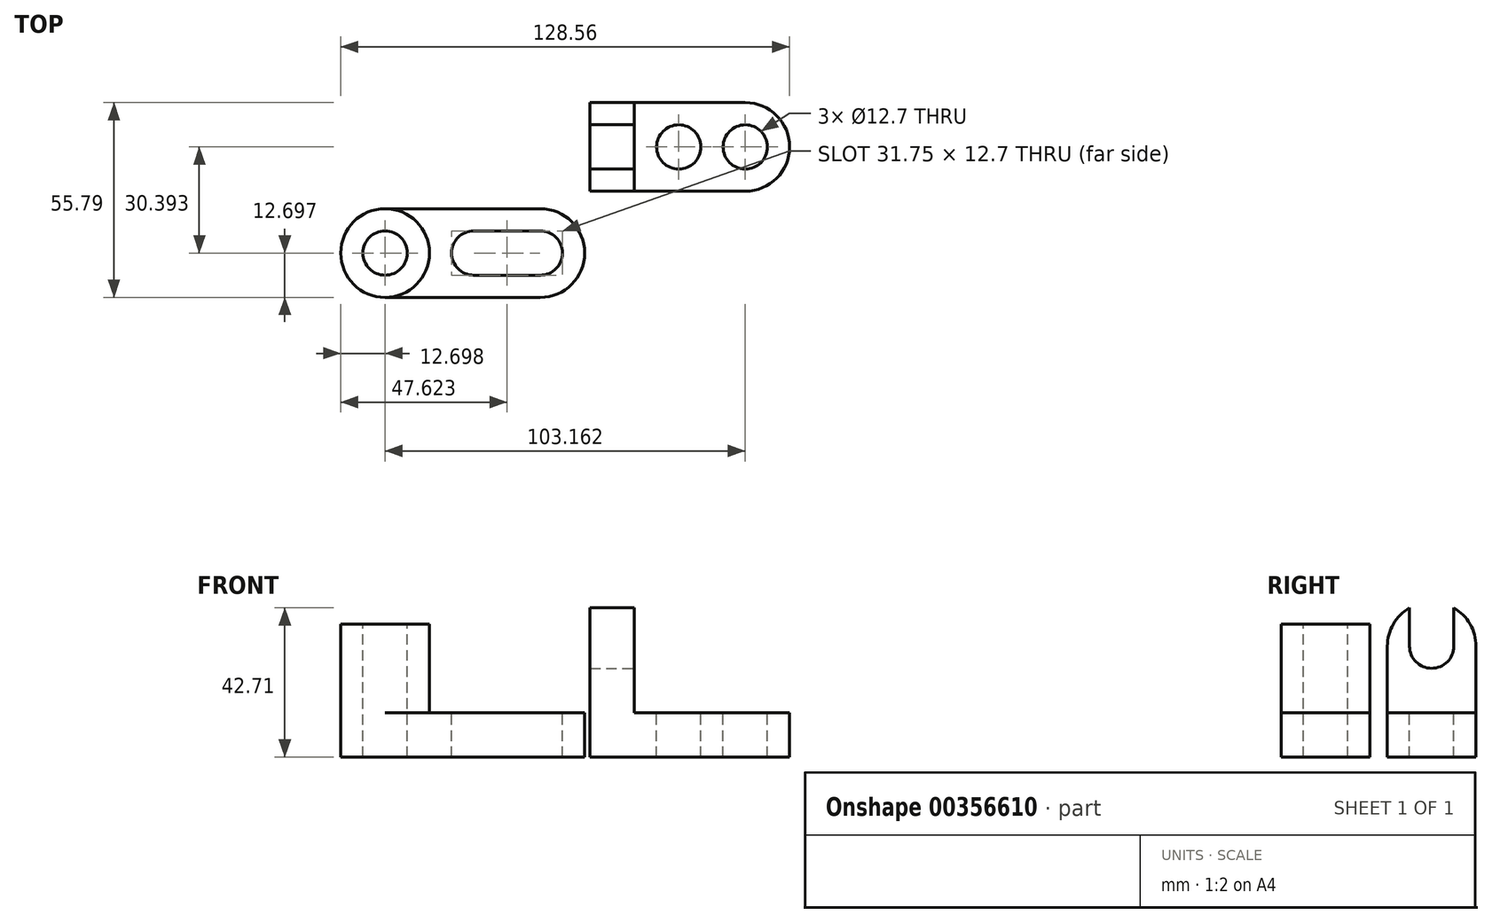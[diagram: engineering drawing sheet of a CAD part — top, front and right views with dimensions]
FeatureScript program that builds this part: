
annotation { "Feature Type Name" : "Feature", "Feature Type Description" : "" }
export const myFeature = defineFeature(function(context is Context, id is Id, definition is map)
    precondition{}
    {
        {
            var Q0;
            Q0=qCreatedBy(makeId("Front.planeOp"),FACE);
            var sketch = newSketch(context, id + "F0", { "sketchPlane" : qUnion([Q0])});
            skLineSegment(sketch, "E0", {"start": v(0, 0) * mm, "end": v(0, 44.45) * mm});
            skLineSegment(sketch, "E1", {"start": v(0, 44.45) * mm, "end": v(12.7, 44.45) * mm});
            skLineSegment(sketch, "E2", {"start": v(12.7, 44.45) * mm, "end": v(12.7, 12.7) * mm});
            skLineSegment(sketch, "E3", {"start": v(12.7, 12.7) * mm, "end": v(57.15, 12.7) * mm});
            skLineSegment(sketch, "E4", {"start": v(57.15, 12.7) * mm, "end": v(57.15, 0) * mm});
            skLineSegment(sketch, "E5", {"start": v(57.15, 0) * mm, "end": v(0, 0) * mm});
            skSolve(sketch);
        }
        {
            var Q0;
            Q0 = qSketchRegion(id + "F0", true);
            extrude(context, id + "F1", {"entities" : qUnion([Q0]), "depth" : 25.4 * mm});
        }
        {
            var Q0;
            Q0=makeQuery(id+"F1.opExtrude","SWEPT_FACE",FACE,{"disambiguationData":[OSD([sQuery(id+"F0.wireOp",EDGE,"E3")])]});
            var sketch = newSketch(context, id + "F2", { "sketchPlane" : qUnion([Q0])});
            skCircle(sketch, "E6", {"center": v(25.4, -12.7) * mm, "radius": 6.35 * mm});
            skCircle(sketch, "E7", {"center": v(44.45, -12.7) * mm, "radius": 6.35 * mm});
            skArc(sketch, "E8", {"start": v(44.45, -25.4) * mm, "mid": v(57.15, -12.7) * mm, "end": v(44.45, 0) * mm});
            skSolve(sketch);
        }
        {
            var Q0;
            Q0=makeQuery(id+"F2.imprint","IMPRINT",FACE,{"disambiguationData":[TD([[makeQuery(id+"F2.imprint","IMPRINT",EDGE,{"derivedFrom":sQuery(id+"F2.wireOp",EDGE,"E6")}),1.0]])]});
            var Q1;
            Q1=makeQuery(id+"F2.imprint","IMPRINT",FACE,{"disambiguationData":[TD([[makeQuery(id+"F2.imprint","IMPRINT",EDGE,{"derivedFrom":sQuery(id+"F2.wireOp",EDGE,"E7")}),1.0]])]});
            var Q2;
            {var subQ0=sQuery(id+"F2.wireOp",EDGE,"E8");var subQ1=sQuery(id+"F0.wireOp",EDGE,"E3");var subQ2=makeQuery(id+"F1.opExtrude","CAP_EDGE",EDGE,{"disambiguationData":[OSD([subQ1])],"isStart":true});var subQ3=makeQuery(id+"F2.imprint","INTERSECT",VERTEX,{"derivedFrom":[subQ2,subQ0]});Q2=makeQuery(id+"F2.imprint","IMPRINT",FACE,{"disambiguationData":[TD([[makeQuery(id+"F2.imprint","IMPRINT",EDGE,{"disambiguationData":[TD([[subQ3,1.0]])],"derivedFrom":subQ0}),-1.0]])]});}
            var Q3;
            {var subQ0=sQuery(id+"F2.wireOp",EDGE,"E8");var subQ1=sQuery(id+"F0.wireOp",EDGE,"E3");var subQ2=makeQuery(id+"F1.opExtrude","CAP_EDGE",EDGE,{"disambiguationData":[OSD([subQ1])],"isStart":false});var subQ3=makeQuery(id+"F2.imprint","INTERSECT",VERTEX,{"derivedFrom":[subQ2,subQ0]});Q3=makeQuery(id+"F2.imprint","IMPRINT",FACE,{"disambiguationData":[TD([[makeQuery(id+"F2.imprint","IMPRINT",EDGE,{"disambiguationData":[TD([[subQ3,-1.0]])],"derivedFrom":subQ0}),-1.0]])]});}
            extrude(context, id + "F3", {"entities" : qUnion([Q0, Q1, Q2, Q3]), "operationType" : NewBodyOperationType.REMOVE, "oppositeDirection" : true, "depth" : 12.7 * mm});
        }
        {
            var Q0;
            Q0=makeQuery(id+"F1.opExtrude","SWEPT_FACE",FACE,{"disambiguationData":[OSD([sQuery(id+"F0.wireOp",EDGE,"E2")])]});
            var sketch = newSketch(context, id + "F4", { "sketchPlane" : qUnion([Q0])});
            skCircle(sketch, "E9", {"center": v(-12.7, 31.75) * mm, "radius": 6.35 * mm});
            skLineSegment(sketch, "E10", {"start": v(-19.05, 31.75) * mm, "end": v(-19.05, 44.45) * mm});
            skLineSegment(sketch, "E11", {"start": v(-6.35, 31.75) * mm, "end": v(-6.35, 44.45) * mm});
            skArc(sketch, "E12", {"start": v(0, 31.75) * mm, "mid": v(-12.7, 44.4) * mm, "end": v(-25.4, 31.75) * mm});
            skSolve(sketch);
        }
        {
            var Q0;
            Q0 = qSketchRegion(id + "F4", true);
            var Q1;
            {var subQ0=sQuery(id+"F4.wireOp",EDGE,"E10");Q1=makeQuery(id+"F4.imprint","IMPRINT",FACE,{"disambiguationData":[TD([[makeQuery(id+"F4.imprint","IMPRINT",EDGE,{"derivedFrom":subQ0}),-1.0]])]});}
            var Q2;
            {var subQ1=sQuery(id+"F0.wireOp",EDGE,"E2");var subQ4=sQuery(id+"F4.wireOp",EDGE,"E12");var subQ6=makeQuery(id+"F1.opExtrude","CAP_EDGE",EDGE,{"disambiguationData":[OSD([subQ1])],"isStart":true});var subQ8=makeQuery(id+"F4.imprint","INTERSECT",VERTEX,{"derivedFrom":[subQ6,subQ4]});Q2=makeQuery(id+"F4.imprint","IMPRINT",FACE,{"disambiguationData":[TD([[makeQuery(id+"F4.imprint","IMPRINT",EDGE,{"disambiguationData":[TD([[subQ8,-1.0]])],"derivedFrom":subQ4}),-1.0]])]});}
            var Q3;
            {var subQ1=sQuery(id+"F0.wireOp",EDGE,"E2");var subQ4=sQuery(id+"F4.wireOp",EDGE,"E12");var subQ6=makeQuery(id+"F1.opExtrude","CAP_EDGE",EDGE,{"disambiguationData":[OSD([subQ1])],"isStart":false});var subQ7=makeQuery(id+"F4.imprint","INTERSECT",VERTEX,{"derivedFrom":[subQ6,subQ4]});Q3=makeQuery(id+"F4.imprint","IMPRINT",FACE,{"disambiguationData":[TD([[makeQuery(id+"F4.imprint","IMPRINT",EDGE,{"disambiguationData":[TD([[subQ7,1.0]])],"derivedFrom":subQ4}),-1.0]])]});}
            extrude(context, id + "F5", {"entities" : qUnion([Q0, Q1, Q2, Q3]), "operationType" : NewBodyOperationType.REMOVE, "oppositeDirection" : true, "depth" : 12.7 * mm});
        }
        {
            var Q0;
            Q0=qCreatedBy(makeId("Top.planeOp"),FACE);
            var sketch = newSketch(context, id + "F6", { "sketchPlane" : qUnion([Q0])});
            skLineSegment(sketch, "E13.bottom", {"start": v(-71.41, -30.4) * mm, "end": v(-1.56, -30.4) * mm});
            skLineSegment(sketch, "E13.top", {"start": v(-71.41, -55.8) * mm, "end": v(-1.56, -55.8) * mm});
            skLineSegment(sketch, "E13.left", {"start": v(-71.41, -30.4) * mm, "end": v(-71.41, -55.8) * mm});
            skLineSegment(sketch, "E13.right", {"start": v(-1.56, -30.4) * mm, "end": v(-1.56, -55.8) * mm});
            skSolve(sketch);
        }
        {
            var Q0;
            Q0 = qSketchRegion(id + "F6", true);
            extrude(context, id + "F7", {"entities" : qUnion([Q0]), "depth" : 12.7 * mm});
        }
        {
            var Q0;
            Q0=makeQuery(id+"F7.opExtrude","CAP_FACE",FACE,{"disambiguationData":[OSD([sQuery(id+"F6.wireOp",EDGE,"E13.bottom"),sQuery(id+"F6.wireOp",EDGE,"E13.top"),sQuery(id+"F6.wireOp",EDGE,"E13.left"),sQuery(id+"F6.wireOp",EDGE,"E13.right")])],"isStart":false});
            var sketch = newSketch(context, id + "F8", { "sketchPlane" : qUnion([Q0])});
            skCircle(sketch, "E14", {"center": v(-14.26, -43.1) * mm, "radius": 6.35 * mm});
            skPoint(sketch, "E14.centerSnap0", {"position": v(-1.56, -43.1) * mm});
            skCircle(sketch, "E15", {"center": v(-33.31, -43.1) * mm, "radius": 6.35 * mm});
            skCircle(sketch, "E16", {"center": v(-58.71, -43.1) * mm, "radius": 12.7 * mm});
            skArc(sketch, "E17", {"start": v(-14.26, -55.8) * mm, "mid": v(-1.56, -43.1) * mm, "end": v(-14.26, -30.4) * mm});
            skCircle(sketch, "E18", {"center": v(-58.71, -43.1) * mm, "radius": 6.35 * mm});
            skLineSegment(sketch, "E19", {"start": v(-33.31, -36.74) * mm, "end": v(-14.26, -36.74) * mm});
            skLineSegment(sketch, "E20", {"start": v(-33.31, -49.44) * mm, "end": v(-14.26, -49.44) * mm});
            skSolve(sketch);
        }
        {
            var Q0;
            Q0=makeQuery(id+"F8.imprint","IMPRINT",FACE,{"disambiguationData":[TD([[makeQuery(id+"F8.imprint","IMPRINT",EDGE,{"derivedFrom":sQuery(id+"F8.wireOp",EDGE,"E15")}),1.0]])]});
            var Q1;
            Q1=makeQuery(id+"F8.imprint","IMPRINT",FACE,{"disambiguationData":[TD([[makeQuery(id+"F8.imprint","IMPRINT",EDGE,{"derivedFrom":sQuery(id+"F8.wireOp",EDGE,"E14")}),1.0]])]});
            var Q2;
            {var subQ0=sQuery(id+"F8.wireOp",EDGE,"E17");var subQ1=makeQuery(id+"F7.opExtrude","CAP_EDGE",EDGE,{"disambiguationData":[OSD([sQuery(id+"F6.wireOp",EDGE,"E13.bottom")])],"isStart":false});var subQ2=makeQuery(id+"F8.imprint","INTERSECT",VERTEX,{"derivedFrom":[subQ1,subQ0]});Q2=makeQuery(id+"F8.imprint","IMPRINT",FACE,{"disambiguationData":[TD([[makeQuery(id+"F8.imprint","IMPRINT",EDGE,{"disambiguationData":[TD([[subQ2,1.0]])],"derivedFrom":subQ0}),-1.0]])]});}
            var Q3;
            {var subQ0=sQuery(id+"F8.wireOp",EDGE,"E17");var subQ1=makeQuery(id+"F7.opExtrude","CAP_EDGE",EDGE,{"disambiguationData":[OSD([sQuery(id+"F6.wireOp",EDGE,"E13.top")])],"isStart":false});var subQ2=makeQuery(id+"F8.imprint","INTERSECT",VERTEX,{"derivedFrom":[subQ1,subQ0]});Q3=makeQuery(id+"F8.imprint","IMPRINT",FACE,{"disambiguationData":[TD([[makeQuery(id+"F8.imprint","IMPRINT",EDGE,{"disambiguationData":[TD([[subQ2,-1.0]])],"derivedFrom":subQ0}),-1.0]])]});}
            var Q4;
            {var subQ0=sQuery(id+"F8.wireOp",EDGE,"E16");var subQ1=makeQuery(id+"F7.opExtrude","CAP_EDGE",EDGE,{"disambiguationData":[OSD([sQuery(id+"F6.wireOp",EDGE,"E13.left")])],"isStart":false});var subQ2=makeQuery(id+"F8.imprint","INTERSECT",VERTEX,{"derivedFrom":[subQ1,subQ0]});Q4=makeQuery(id+"F8.imprint","IMPRINT",FACE,{"disambiguationData":[TD([[makeQuery(id+"F8.imprint","IMPRINT",EDGE,{"disambiguationData":[TD([[subQ2,1.0]])],"derivedFrom":subQ0}),-1.0]])]});}
            var Q5;
            {var subQ0=sQuery(id+"F8.wireOp",EDGE,"E16");var subQ1=makeQuery(id+"F7.opExtrude","CAP_EDGE",EDGE,{"disambiguationData":[OSD([sQuery(id+"F6.wireOp",EDGE,"E13.left")])],"isStart":false});var subQ2=makeQuery(id+"F8.imprint","INTERSECT",VERTEX,{"derivedFrom":[subQ1,subQ0]});Q5=makeQuery(id+"F8.imprint","IMPRINT",FACE,{"disambiguationData":[TD([[makeQuery(id+"F8.imprint","IMPRINT",EDGE,{"disambiguationData":[TD([[subQ2,-1.0]])],"derivedFrom":subQ0}),-1.0]])]});}
            var Q6;
            Q6=makeQuery(id+"F8.imprint","IMPRINT",FACE,{"disambiguationData":[TD([[makeQuery(id+"F8.imprint","IMPRINT",EDGE,{"derivedFrom":sQuery(id+"F8.wireOp",EDGE,"E18")}),1.0]])]});
            var Q7;
            {var subQ0=sQuery(id+"F8.wireOp",EDGE,"E19");Q7=makeQuery(id+"F8.imprint","IMPRINT",FACE,{"disambiguationData":[TD([[makeQuery(id+"F8.imprint","IMPRINT",EDGE,{"derivedFrom":subQ0}),-1.0]])]});}
            extrude(context, id + "F9", {"entities" : qUnion([Q0, Q1, Q2, Q3, Q4, Q5, Q6, Q7]), "operationType" : NewBodyOperationType.REMOVE, "oppositeDirection" : true, "depth" : 12.7 * mm});
        }
        {
            var Q0;
            Q0=makeQuery(id+"F8.imprint","IMPRINT",FACE,{"disambiguationData":[TD([[makeQuery(id+"F8.imprint","IMPRINT",EDGE,{"derivedFrom":sQuery(id+"F8.wireOp",EDGE,"E18")}),-1.0]])]});
            extrude(context, id + "F10", {"entities" : qUnion([Q0]), "operationType" : NewBodyOperationType.ADD, "depth" : 25.4 * mm});
        }
    });
